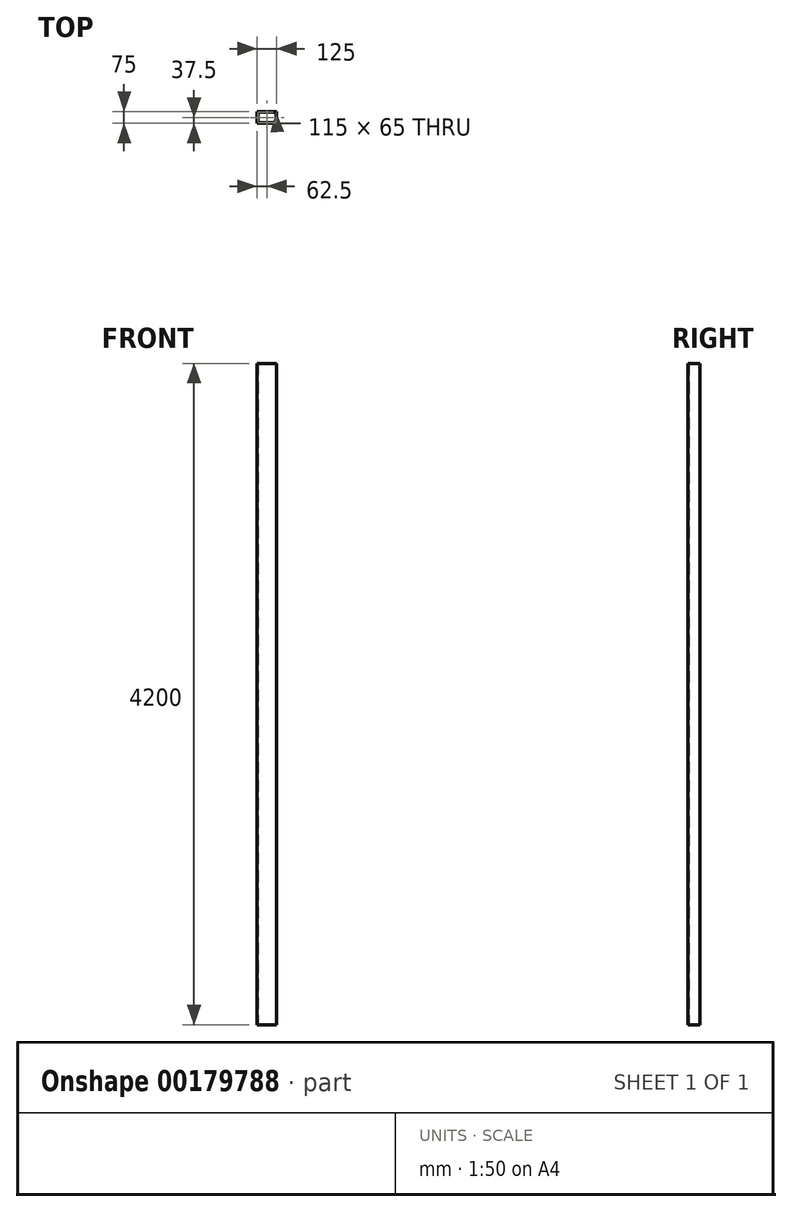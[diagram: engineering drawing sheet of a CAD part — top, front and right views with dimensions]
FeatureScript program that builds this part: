
annotation { "Feature Type Name" : "Feature", "Feature Type Description" : "" }
export const myFeature = defineFeature(function(context is Context, id is Id, definition is map)
    precondition{}
    {
        {
            var Q0;
            Q0=qCreatedBy(makeId("Top.planeOp"),FACE);
            var sketch = newSketch(context, id + "F0", { "sketchPlane" : qUnion([Q0])});
            skLineSegment(sketch, "E0.bottom", {"start": v(-62.5, -37.5) * mm, "end": v(62.5, -37.5) * mm});
            skLineSegment(sketch, "E0.top", {"start": v(-62.5, 37.5) * mm, "end": v(62.5, 37.5) * mm});
            skLineSegment(sketch, "E0.left", {"start": v(-62.5, -37.5) * mm, "end": v(-62.5, 37.5) * mm});
            skLineSegment(sketch, "E0.right", {"start": v(62.5, -37.5) * mm, "end": v(62.5, 37.5) * mm});
            skPoint(sketch, "E0.middle", {"position": v(0, 0) * mm});
            skLineSegment(sketch, "E1.bottom", {"start": v(57.5, -32.5) * mm, "end": v(-57.5, -32.5) * mm});
            skLineSegment(sketch, "E1.top", {"start": v(57.5, 32.5) * mm, "end": v(-57.5, 32.5) * mm});
            skLineSegment(sketch, "E1.left", {"start": v(57.5, -32.5) * mm, "end": v(57.5, 32.5) * mm});
            skLineSegment(sketch, "E1.right", {"start": v(-57.5, -32.5) * mm, "end": v(-57.5, 32.5) * mm});
            skSolve(sketch);
        }
        {
            var Q0;
            Q0 = qSketchRegion(id + "F0", true);
            extrude(context, id + "F1", {"entities" : qUnion([Q0]), "depth" : 4200 * mm});
        }
    });
